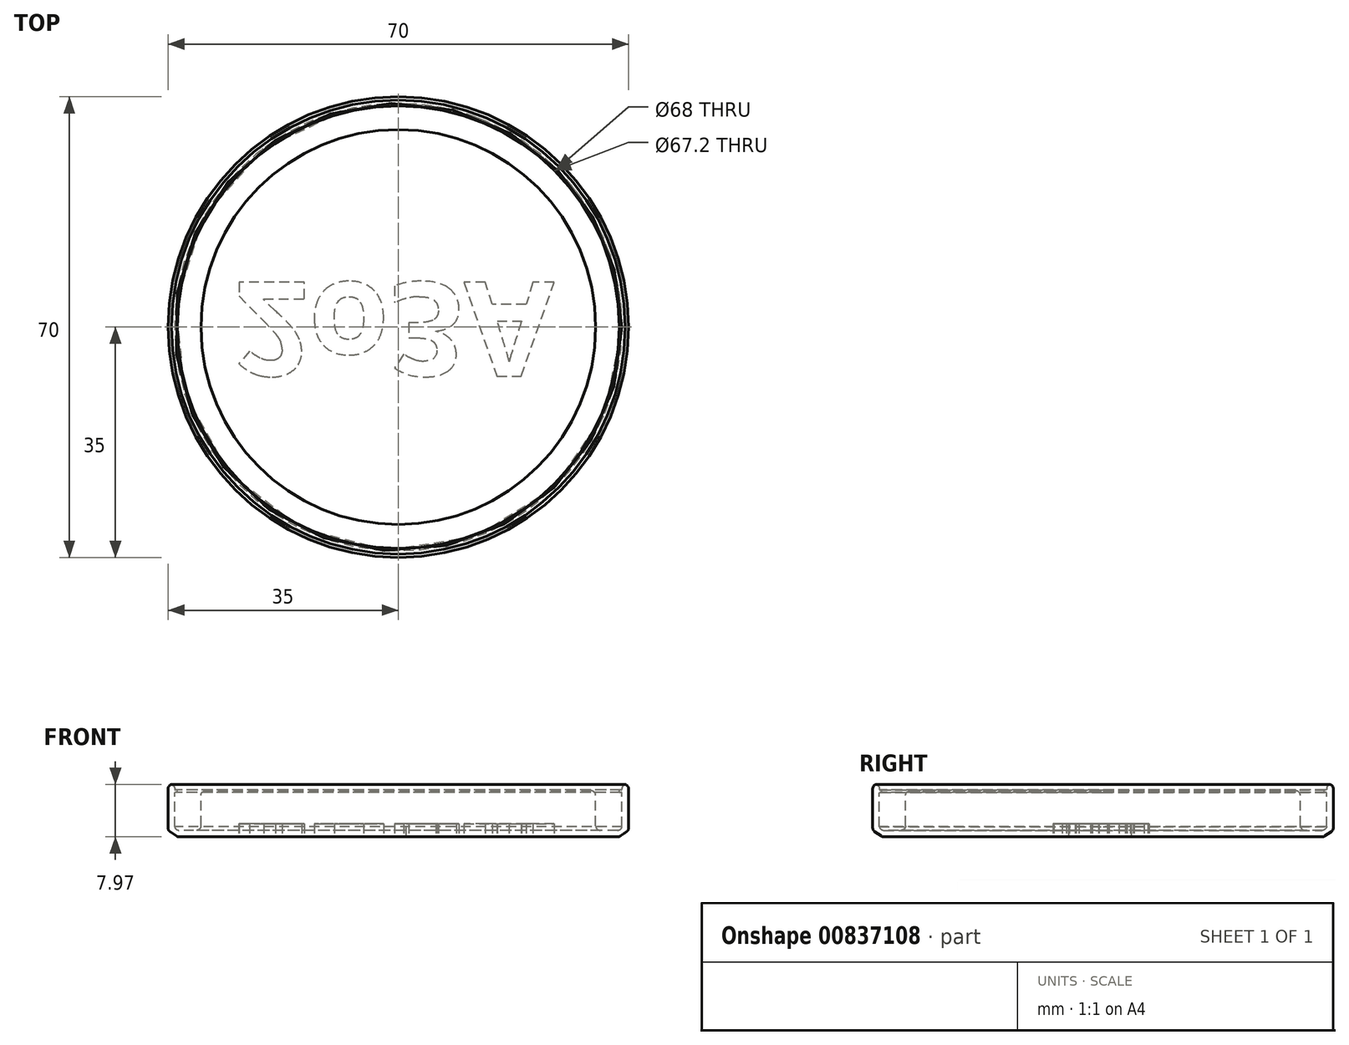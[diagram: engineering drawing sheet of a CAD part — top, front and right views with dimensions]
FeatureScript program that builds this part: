
annotation { "Feature Type Name" : "Feature", "Feature Type Description" : "" }
export const myFeature = defineFeature(function(context is Context, id is Id, definition is map)
    precondition{}
    {
        {
            var Q0;
            Q0=qCreatedBy(makeId("Front.planeOp"),FACE);
            var sketch = newSketch(context, id + "F0", { "sketchPlane" : qUnion([Q0])});
            skLineSegment(sketch, "E0", {"start": v(-35, 7.3) * mm, "end": v(-35, 1.37) * mm});
            skLineSegment(sketch, "E1", {"start": v(-30, 0) * mm, "end": v(0, 0) * mm});
            skLineSegment(sketch, "E2", {"start": v(-34.68, 8) * mm, "end": v(-34.3, 8) * mm});
            skLineSegment(sketch, "E3", {"start": v(0, 2.2) * mm, "end": v(0, 0) * mm});
            skLineSegment(sketch, "E4", {"start": v(-33.32, 1) * mm, "end": v(-30.7, 1) * mm});
            skLineSegment(sketch, "E5", {"start": v(-30, 1.7) * mm, "end": v(-30, 6.3) * mm});
            skLineSegment(sketch, "E6", {"start": v(-29.3, 7) * mm, "end": v(0, 7) * mm});
            skLineSegment(sketch, "E7", {"start": v(0, 7) * mm, "end": v(0, 2.2) * mm});
            skLineSegment(sketch, "E8", {"start": v(-34.7, 0.8) * mm, "end": v(-33.71, 0.12) * mm});
            skLineSegment(sketch, "E9", {"start": v(-33.32, 0) * mm, "end": v(-30, 0) * mm});
            skPoint(sketch, "E10.visualSharp", {"position": v(-35, 8) * mm});
            skArc(sketch, "E10.filletArc", {"start": v(-34.3, 8) * mm, "mid": v(-34.8, 7.8) * mm, "end": v(-35, 7.3) * mm});
            skPoint(sketch, "E11.visualSharp", {"position": v(-33.98, 8) * mm});
            skArc(sketch, "E11.filletArc", {"start": v(-33.98, 7.24) * mm, "mid": v(-34.17, 7.77) * mm, "end": v(-34.68, 8) * mm});
            skPoint(sketch, "E12.visualSharp", {"position": v(-35, 1) * mm});
            skArc(sketch, "E12.filletArc", {"start": v(-35, 1.37) * mm, "mid": v(-34.92, 1.04) * mm, "end": v(-34.7, 0.8) * mm});
            skPoint(sketch, "E13.visualSharp", {"position": v(-33.53, 0) * mm});
            skArc(sketch, "E13.filletArc", {"start": v(-33.71, 0.12) * mm, "mid": v(-33.52, 0.03) * mm, "end": v(-33.32, 0) * mm});
            skPoint(sketch, "E14.visualSharp", {"position": v(-33.06, 1) * mm});
            skArc(sketch, "E14.filletArc", {"start": v(-34, 1.54) * mm, "mid": v(-33.75, 1.15) * mm, "end": v(-33.32, 1) * mm});
            skPoint(sketch, "E15.visualSharp", {"position": v(-30, 1) * mm});
            skArc(sketch, "E15.filletArc", {"start": v(-30.7, 1) * mm, "mid": v(-30.2, 1.2) * mm, "end": v(-30, 1.7) * mm});
            skPoint(sketch, "E16.visualSharp", {"position": v(-30, 7) * mm});
            skArc(sketch, "E16.filletArc", {"start": v(-29.3, 7) * mm, "mid": v(-29.8, 6.8) * mm, "end": v(-30, 6.3) * mm});
            skLineSegment(sketch, "E17", {"start": v(-33.9, 7.14) * mm, "end": v(-33.71, 7.14) * mm});
            skLineSegment(sketch, "E18", {"start": v(-33.6, 7.03) * mm, "end": v(-33.6, 6.85) * mm});
            skLineSegment(sketch, "E19", {"start": v(-33.71, 6.74) * mm, "end": v(-33.89, 6.74) * mm});
            skLineSegment(sketch, "E20", {"start": v(-34, 6.63) * mm, "end": v(-34, 1.54) * mm});
            skPoint(sketch, "E21.visualSharp", {"position": v(-33.6, 6.74) * mm});
            skArc(sketch, "E21.filletArc", {"start": v(-33.71, 6.74) * mm, "mid": v(-33.63, 6.77) * mm, "end": v(-33.6, 6.85) * mm});
            skPoint(sketch, "E22.visualSharp", {"position": v(-33.6, 7.14) * mm});
            skArc(sketch, "E22.filletArc", {"start": v(-33.6, 7.03) * mm, "mid": v(-33.63, 7.1) * mm, "end": v(-33.71, 7.14) * mm});
            skPoint(sketch, "E23.visualSharp", {"position": v(-34, 7.14) * mm});
            skArc(sketch, "E23.filletArc", {"start": v(-33.98, 7.24) * mm, "mid": v(-33.96, 7.17) * mm, "end": v(-33.9, 7.14) * mm});
            skPoint(sketch, "E24.visualSharp", {"position": v(-34, 6.74) * mm});
            skArc(sketch, "E24.filletArc", {"start": v(-33.89, 6.74) * mm, "mid": v(-33.97, 6.7) * mm, "end": v(-34, 6.63) * mm});
            skSolve(sketch);
        }
        {
            var Q0;
            Q0=makeQuery(id+"F0.imprint","IMPRINT",FACE,{"disambiguationData":[TD([[makeQuery(id+"F0.imprint","IMPRINT",EDGE,{"derivedFrom":sQuery(id+"F0.wireOp",EDGE,"E0")}),1.0]])]});
            var Q1;
            Q1=sQuery(id+"F0.wireOp",EDGE,"E3");
            revolve(context, id + "F1", {"surfaceOperationType" : NewSurfaceOperationType.NEW, "entities" : qUnion([Q0]), "axis" : qUnion([Q1]), "revolveType" : RevolveType.FULL});
        }
        {
            var Q0;
            Q0=makeQuery(id+"F1.opRevolve","SWEPT_FACE",FACE,{"disambiguationData":[OSD([sQuery(id+"F0.wireOp",EDGE,"E1"),sQuery(id+"F0.wireOp",EDGE,"E9")])]});
            var sketch = newSketch(context, id + "F2", { "sketchPlane" : qUnion([Q0])});
            skText(sketch, "E25", { "text": "2o3A", "fontName": "OpenSans-Bold.ttf"});
            const initialGuessF2  = {"E25": [-0.025, -0.0068, 1, 0, 0.01431]};
            skSetInitialGuess(sketch, initialGuessF2);
            skSolve(sketch);
        }
        {
            var Q0;
            Q0 = qSketchRegion(id + "F2", true);
            extrude(context, id + "F3", {"entities" : qUnion([Q0]), "operationType" : NewBodyOperationType.REMOVE, "oppositeDirection" : true, "depth" : 2 * mm, "offsetDistance" : 25 * mm});
        }
    });
